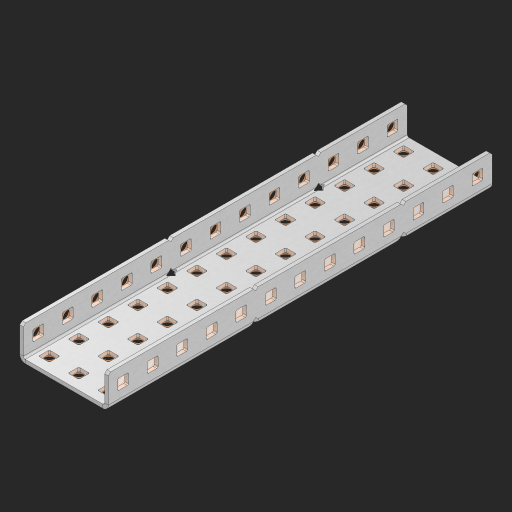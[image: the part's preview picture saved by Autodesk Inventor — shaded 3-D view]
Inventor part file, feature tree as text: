
AUTODESK INVENTOR PART (.ipt)
format: ipt  version: 2023 (Build 270158000, 158)  size: 1,049,088 bytes
history: native  units: in
note: dims shown in document units (in); Inventor stores cm internally (conversion verified against a paired STEP export)
features: other x70, extrude x64, sheet_metal_op x10, sketch x8, mirror x1, pattern_linear x1, chamfer x1
ambient origin geometry x8: Origin, YZ Plane, XZ Plane, XY Plane, X Axis, Y Axis, Z Axis, Center Point
bodies: Solid1 (feature_tree), Body (feature_tree)
feature tree (155):
  other  "Flange Pattern Plane"
  sheet_metal_op  "Flange Pattern"
  sheet_metal_op  "Body Pattern"
  other  "Arc Length"
  mirror  "Notch Mirror"
  pattern_linear  "Notch Pattern"  Spacing1=0.25in  [1 undecoded]
  chamfer  "End Chamfer"
  extrude  "Half Cut"  Depth=0.0625in
  sketch  "Sketch1"  dims[d0=1.5in]
  other  "Plate1"
  sketch  "Sketch2"  dims[d1=6.5in]
  other  "Plate2"
  sheet_metal_op  "Bend1"
  sheet_metal_op  "Corner1"
  sketch  "Sketch3"  dims[d2=0.0625in]
  other  "Flange Pattern Sketch"
  sketch  "Sketch7"  dims[d3=0.0625in]
  other  "Srf1"
  other  "Srf2"
  sketch  "Sketch8"  dims[d4=0.0312in]
  sketch  "Sketch9"  dims[d5=0.125in]
  other  "Srf91"
  sheet_metal_op  "Body Pattern Sketch"
  other  "Srf92"
  sketch  "Sketch13"  dims[d6=0.0625in]
  sketch  "Sketch14"  dims[d7=0.5in d8=90.0deg d9=0.0312in d10=0.25in d11=0.0625in d12=0.0625in d16=0.182in d17=0.02in d18=0.0625in d19=0.0in d20=0.25in d21=0.25in d46=0.172in d47=1.0in d48=0.0in d49=0.182in d50=0.02in d51=0.25in d52=0.25in d53=0.0625in d54=0.0in d55=0.172in d56=1.0in d57=0.0in d60=5.1181in d62=0.5in d63=1.1811in d65=0.5in d85=0.1473in d86=0.1782in d88=0.04in d89=0.0625in d90=0.0in d91=0.04in d92=0.0491in d95=2.5in d96=0.04in d97=0.25in d98=45.0deg d101=0.0in d102=2.497in d131=1.5in d132=5.1181in d134=0.5in d139=0.5in]
  other  "Srf856"
  other  "Srf1310"
  other  "Srf1311"
  other  "Srf1312"
  other  "Srf1376"
  other  "Srf1377"
  other  "Srf1728"
  other  "Srf1755"
  other  "Srf1878"
  other  "Srf1879"
  other  "Srf1880"
  other  "Srf1881"
  other  "Srf1882"
  other  "Srf1883"
  other  "Srf1884"
  other  "Srf1885"
  other  "Srf1886"
  other  "Srf1887"
  other  "Srf1888"
  other  "Srf1889"
  other  "Srf1890"
  other  "Srf1891"
  other  "Srf1892"
  other  "Srf1893"
  other  "Srf1894"
  other  "Srf1895"
  other  "Srf1896"
  other  "Srf1897"
  other  "Srf1942"
  other  "Srf1943"
  other  "Srf1944"
  other  "Srf1945"
  other  "Srf1946"
  other  "Srf1947"
  other  "Srf1948"
  other  "Srf1949"
  other  "Srf1950"
  other  "Srf1951"
  other  "Srf1952"
  other  "Srf1953"
  other  "Srf1954"
  other  "Srf1955"
  other  "Srf1956"
  other  "Srf1957"
  other  "Srf1958"
  other  "Srf1959"
  other  "Srf1960"
  other  "Srf1961"
  other  "Srf1962"
  other  "Srf1963"
  other  "Srf1964"
  other  "Srf1965"
  other  "Srf1966"
  other  "Srf1967"
  other  "Srf1968"
  other  "Srf1969"
  other  "Srf1970"
  other  "Srf1971"
  other  "Srf1972"
  other  "Srf1973"
  other  "Srf1974"
  sheet_metal_op  "Flange Stamp"
  sheet_metal_op  "Flange Circle"
  sheet_metal_op  "Body Stamp"
  sheet_metal_op  "Body Circle"
  sheet_metal_op  "Notch"
  extrude  "ExtrusionSrf2"  Depth=0.0625in
  extrude  "ExtrusionSrf92"  Depth=1.5in
  extrude  "ExtrusionSrf856"  Depth=0.02in
  extrude  "ExtrusionSrf1310"  Depth=0.0625in
  extrude  "ExtrusionSrf1311"  TaperAngle=0.0deg  [1 undecoded]
  extrude  "ExtrusionSrf1312"  Depth=0.25in
  extrude  "ExtrusionSrf1376"  Depth=0.25in
  extrude  "ExtrusionSrf1377"  Depth=1.5in
  extrude  "ExtrusionSrf1728"  Depth=1.5in TaperAngle=0.0deg
  extrude  "ExtrusionSrf1755"  Depth=1.5in
  extrude  "ExtrusionSrf1878"  Depth=0.02in
  extrude  "ExtrusionSrf1879"  Depth=0.25in
  extrude  "ExtrusionSrf1880"  Depth=0.25in
  extrude  "ExtrusionSrf1881"  Depth=0.0625in
  extrude  "ExtrusionSrf1882"  TaperAngle=0.0deg  [1 undecoded]
  extrude  "ExtrusionSrf1883"  Depth=1.5in
  extrude  "ExtrusionSrf1884"  Depth=1.5in TaperAngle=0.0deg
  extrude  "ExtrusionSrf1885"  Depth=1.5in
  extrude  "ExtrusionSrf1886"  Depth=1.5in
  extrude  "ExtrusionSrf1887"  Depth=1.5in
  extrude  "ExtrusionSrf1888"  Depth=1.5in
  extrude  "ExtrusionSrf1889"  Depth=1.5in
  extrude  "ExtrusionSrf1890"  Depth=0.0625in
  extrude  "ExtrusionSrf1891"  TaperAngle=0.0deg  [1 undecoded]
  extrude  "ExtrusionSrf1892"  Depth=1.5in
  extrude  "ExtrusionSrf1893"  Depth=1.5in
  extrude  "ExtrusionSrf1894"  Depth=1.5in
  extrude  "ExtrusionSrf1895"  Depth=0.25in TaperAngle=45.0deg
  extrude  "ExtrusionSrf1896"  TaperAngle=0.0deg  [1 undecoded]
  extrude  "ExtrusionSrf1897"  Depth=1.5in
  extrude  "ExtrusionSrf1942"  Depth=1.5in
  extrude  "ExtrusionSrf1943"  Depth=1.5in
  extrude  "ExtrusionSrf1944"  Depth=1.5in
  extrude  "ExtrusionSrf1945"  Depth=1.5in
  extrude  "ExtrusionSrf1946"  [1 undecoded]
  extrude  "ExtrusionSrf1947"  [1 undecoded]
  extrude  "ExtrusionSrf1948"  [1 undecoded]
  extrude  "ExtrusionSrf1949"  [1 undecoded]
  extrude  "ExtrusionSrf1950"  [1 undecoded]
  extrude  "ExtrusionSrf1951"  [1 undecoded]
  extrude  "ExtrusionSrf1952"  [1 undecoded]
  extrude  "ExtrusionSrf1953"  [1 undecoded]
  extrude  "ExtrusionSrf1954"  [1 undecoded]
  extrude  "ExtrusionSrf1955"  [1 undecoded]
  extrude  "ExtrusionSrf1956"  [1 undecoded]
  extrude  "ExtrusionSrf1957"  [1 undecoded]
  extrude  "ExtrusionSrf1958"  [1 undecoded]
  extrude  "ExtrusionSrf1959"  [1 undecoded]
  extrude  "ExtrusionSrf1960"  [1 undecoded]
  extrude  "ExtrusionSrf1961"  [1 undecoded]
  extrude  "ExtrusionSrf1962"  [1 undecoded]
  extrude  "ExtrusionSrf1963"  [1 undecoded]
  extrude  "ExtrusionSrf1964"  [1 undecoded]
  extrude  "ExtrusionSrf1965"  [1 undecoded]
  extrude  "ExtrusionSrf1966"  [1 undecoded]
  extrude  "ExtrusionSrf1967"  [1 undecoded]
  extrude  "ExtrusionSrf1968"  [1 undecoded]
  extrude  "ExtrusionSrf1969"  [1 undecoded]
  extrude  "ExtrusionSrf1970"  [1 undecoded]
  extrude  "ExtrusionSrf1971"  [1 undecoded]
  extrude  "ExtrusionSrf1972"  [1 undecoded]
  extrude  "ExtrusionSrf1973"  [1 undecoded]
  extrude  "ExtrusionSrf1974"  [1 undecoded]
note: 34 required parameter values undecoded (feature->parameter linkage not recoverable at this tier; creation-order binding heuristic only, values carry confidence <= 0.55)
